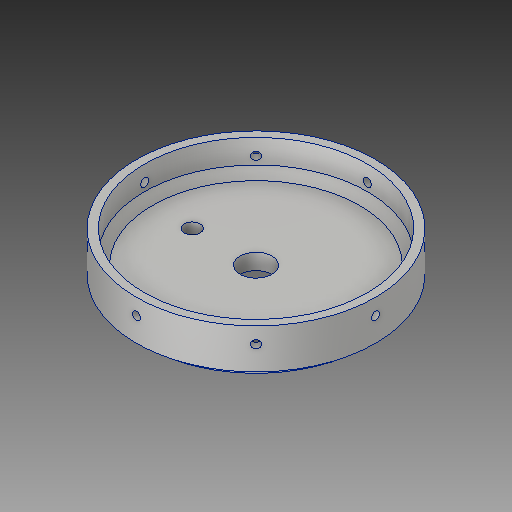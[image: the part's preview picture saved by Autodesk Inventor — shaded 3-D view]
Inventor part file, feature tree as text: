
AUTODESK INVENTOR PART (.ipt)
format: ipt  version: 2017 SP1 (Build 210196100, 196)  size: 184,320 bytes
history: native  units: in
note: dims shown in document units (in); Inventor stores cm internally (conversion verified against a paired STEP export)
features: sketch x5, extrude x4, plane x1, hole x1, pattern_circular x1, chamfer x1
ambient origin geometry x8: Origin, YZ Plane, XZ Plane, XY Plane, X Axis, Y Axis, Z Axis, Center Point
bodies: Solid1 (feature_tree)
feature tree (13):
  extrude  "Extrusion1"  Depth=0.25in TaperAngle=0.0deg
  extrude  "Extrusion2"  Depth=0.25in TaperAngle=0.0deg
  extrude  "Extrusion3"  Depth=7.0in
  plane  "Work Plane1"
  hole  "Hole1"  [1 undecoded]
  pattern_circular  "Circular Pattern1"  Count=8 Angle=360.0deg
  extrude  "Extrusion4"  Depth=0.5in
  chamfer  "Chamfer1"  Distance=1.0in
  sketch  "Sketch1"  dims[d0=6.9in d1=0.25in d2=0.0in]
  sketch  "Sketch2"  dims[d3=7.5in d4=0.25in d5=0.0in]
  sketch  "Sketch3"  dims[d6=7.5in d7=7.0in]
  sketch  "Sketch4"  dims[d8=1.0in d9=0.0in d10=0.75in]
  sketch  "Sketch5"  dims[d11=0.25in d12=0.75in d13=0.375in d14=0.25in d15=0.5635in d16=1.0in d17=0.8108in d18=3.1496in d19=360.0deg d21=0.5in d22=1.0in d23=2.0in d24=0.5in d25=0.0in d26=0.25in d27=0.125in d28=45.0deg]
note: 1 required parameter value undecoded (feature->parameter linkage not recoverable at this tier; creation-order binding heuristic only, values carry confidence <= 0.55)
